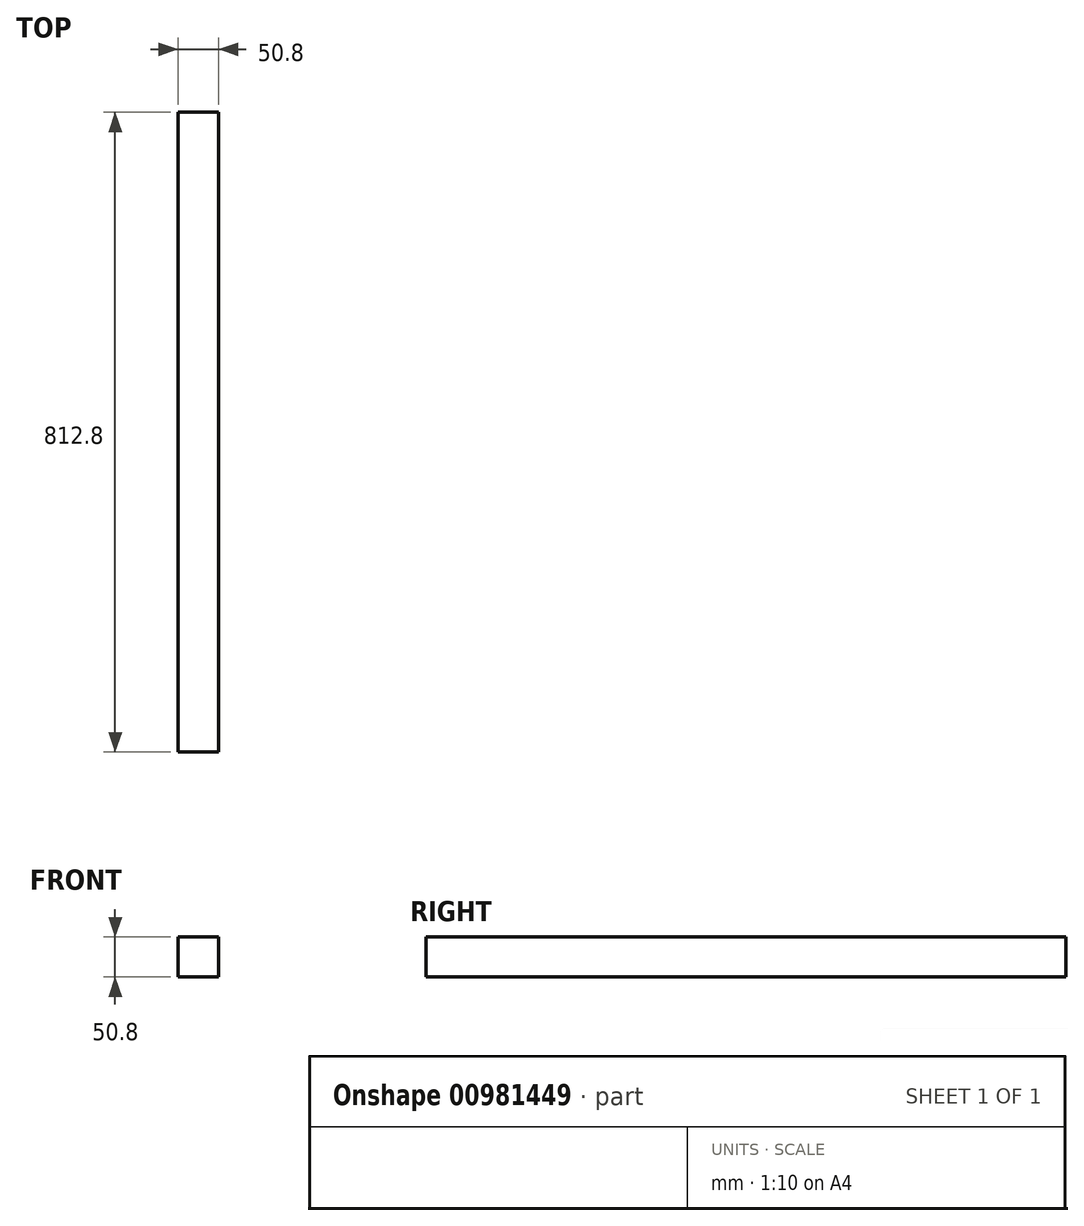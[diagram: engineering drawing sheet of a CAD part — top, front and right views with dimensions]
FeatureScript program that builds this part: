
annotation { "Feature Type Name" : "Feature", "Feature Type Description" : "" }
export const myFeature = defineFeature(function(context is Context, id is Id, definition is map)
    precondition{}
    {
        {
            var Q0;
            Q0=qCreatedBy(makeId("Front.planeOp"),FACE);
            var sketch = newSketch(context, id + "F0", { "sketchPlane" : qUnion([Q0])});
            skLineSegment(sketch, "E0.bottom", {"start": v(-25.4, 25.4) * mm, "end": v(25.4, 25.4) * mm});
            skLineSegment(sketch, "E0.top", {"start": v(-25.4, -25.4) * mm, "end": v(25.4, -25.4) * mm});
            skLineSegment(sketch, "E0.left", {"start": v(-25.4, 25.4) * mm, "end": v(-25.4, -25.4) * mm});
            skLineSegment(sketch, "E0.right", {"start": v(25.4, 25.4) * mm, "end": v(25.4, -25.4) * mm});
            skSolve(sketch);
        }
        {
            var Q0;
            Q0=qSketchRegion(id+"F0",true);
            extrude(context, id + "F1", {"entities" : qUnion([Q0]), "oppositeDirection" : true, "depth" : 812.8 * mm, "offsetDistance" : 25.4 * mm});
        }
    });
